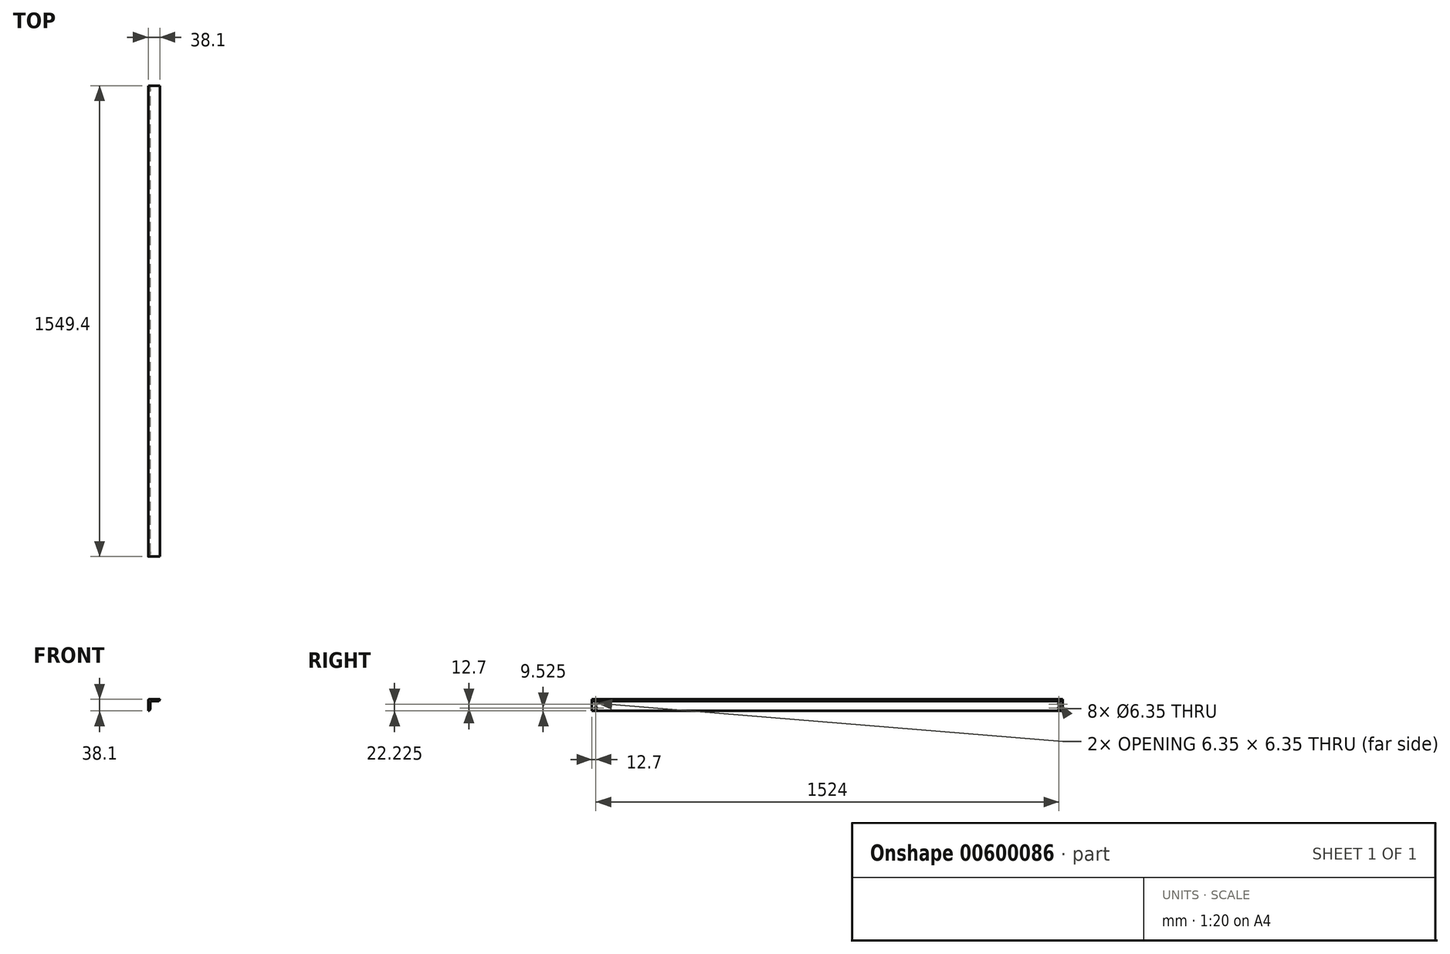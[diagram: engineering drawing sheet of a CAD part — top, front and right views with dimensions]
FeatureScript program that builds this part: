
annotation { "Feature Type Name" : "Feature", "Feature Type Description" : "" }
export const myFeature = defineFeature(function(context is Context, id is Id, definition is map)
    precondition{}
    {
        {
            var Q0;
            Q0=qCreatedBy(makeId("Front.planeOp"),FACE);
            var sketch = newSketch(context, id + "F0", { "sketchPlane" : qUnion([Q0])});
            skLineSegment(sketch, "E0", {"start": v(3.17, 38.1) * mm, "end": v(38.1, 38.1) * mm});
            skLineSegment(sketch, "E1", {"start": v(38.1, 38.1) * mm, "end": v(38.1, 38.1) * mm});
            skLineSegment(sketch, "E2", {"start": v(31.75, 31.75) * mm, "end": v(12.7, 31.75) * mm});
            skLineSegment(sketch, "E3", {"start": v(6.35, 25.4) * mm, "end": v(6.35, 6.35) * mm});
            skLineSegment(sketch, "E4", {"start": v(0, 0) * mm, "end": v(0, 0) * mm});
            skLineSegment(sketch, "E5", {"start": v(0, 0) * mm, "end": v(0, 34.93) * mm});
            skPoint(sketch, "E6.visualSharp", {"position": v(38.1, 31.75) * mm});
            skArc(sketch, "E6.filletArc", {"start": v(31.75, 31.75) * mm, "mid": v(36.24, 33.6) * mm, "end": v(38.1, 38.1) * mm});
            skPoint(sketch, "E7.visualSharp", {"position": v(6.35, 0) * mm});
            skArc(sketch, "E7.filletArc", {"start": v(0, 0) * mm, "mid": v(4.5, 1.86) * mm, "end": v(6.35, 6.35) * mm});
            skPoint(sketch, "E8.visualSharp", {"position": v(6.35, 31.75) * mm});
            skArc(sketch, "E8.filletArc", {"start": v(12.7, 31.75) * mm, "mid": v(8.2, 29.9) * mm, "end": v(6.35, 25.4) * mm});
            skPoint(sketch, "E9.visualSharp", {"position": v(0, 38.1) * mm});
            skArc(sketch, "E9.filletArc", {"start": v(3.17, 38.1) * mm, "mid": v(0.93, 37.17) * mm, "end": v(0, 34.93) * mm});
            skSolve(sketch);
        }
        {
            var Q0;
            Q0 = qSketchRegion(id + "F0", true);
            extrude(context, id + "F1", {"entities" : qUnion([Q0]), "depth" : 1524 * mm, "offsetDistance" : 25.4 * mm, "hasSecondDirection" : true, "secondDirectionOppositeDirection" : true, "secondDirectionDepth" : 25.4 * mm});
        }
        {
            var Q0;
            Q0=qCreatedBy(makeId("Right.planeOp"),FACE);
            var sketch = newSketch(context, id + "F2", { "sketchPlane" : qUnion([Q0])});
            skCircle(sketch, "E10", {"center": v(12.7, 9.53) * mm, "radius": 3.18 * mm});
            skCircle(sketch, "E11", {"center": v(12.7, 22.23) * mm, "radius": 3.18 * mm});
            skCircle(sketch, "E12", {"center": v(-1511.3, 9.53) * mm, "radius": 3.18 * mm});
            skCircle(sketch, "E13", {"center": v(-1511.3, 22.23) * mm, "radius": 3.18 * mm});
            skSolve(sketch);
        }
        {
            var Q0;
            Q0 = qSketchRegion(id + "F2", true);
            extrude(context, id + "F3", {"entities" : qUnion([Q0]), "operationType" : NewBodyOperationType.REMOVE, "depth" : 38.1 * mm, "offsetDistance" : 25.4 * mm});
        }
    });
